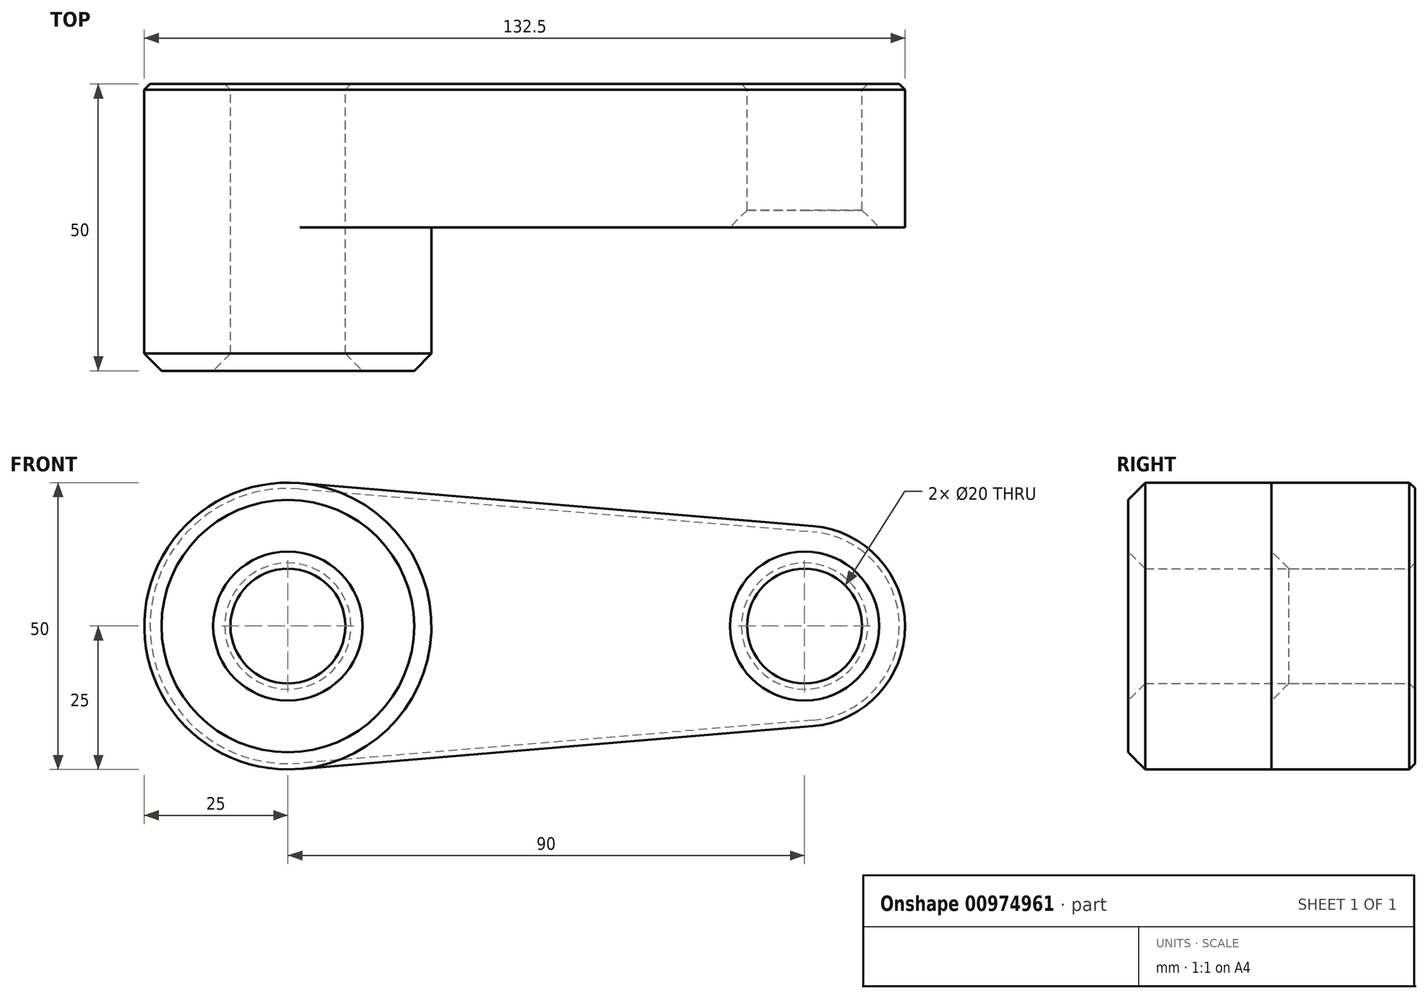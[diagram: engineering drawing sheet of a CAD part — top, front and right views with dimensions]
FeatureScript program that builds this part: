
annotation { "Feature Type Name" : "Feature", "Feature Type Description" : "" }
export const myFeature = defineFeature(function(context is Context, id is Id, definition is map)
    precondition{}
    {
        {
            var Q0;
            Q0=qCreatedBy(makeId("Front.planeOp"),FACE);
            var sketch = newSketch(context, id + "F0", { "sketchPlane" : qUnion([Q0])});
            skCircle(sketch, "E0", {"center": v(0, 0) * mm, "radius": 25 * mm});
            skCircle(sketch, "E1", {"center": v(90, 0) * mm, "radius": 17.5 * mm});
            skLineSegment(sketch, "E2", {"start": v(2.08, 24.91) * mm, "end": v(91.46, 17.44) * mm});
            skLineSegment(sketch, "E3", {"start": v(2.08, -24.91) * mm, "end": v(91.46, -17.44) * mm});
            skCircle(sketch, "E4", {"center": v(0, 0) * mm, "radius": 10 * mm});
            skCircle(sketch, "E5", {"center": v(90, 0) * mm, "radius": 10 * mm});
            skSolve(sketch);
        }
        {
            var Q0;
            Q0=qSketchRegion(id+"F0",true);
            extrude(context, id + "F1", {"entities" : qUnion([Q0]), "depth" : 25 * mm});
        }
        {
            var Q0;
            Q0=makeQuery(id+"F0.imprint","IMPRINT",FACE,{"disambiguationData":[TD([[makeQuery(id+"F0.imprint","IMPRINT",EDGE,{"derivedFrom":sQuery(id+"F0.wireOp",EDGE,"E4")}),-1.0]])]});
            extrude(context, id + "F2", {"entities" : qUnion([Q0]), "operationType" : NewBodyOperationType.ADD, "depth" : 50 * mm});
        }
        {
            var Q0;
            Q0=makeQuery(id+"F2.opExtrude","CAP_EDGE",EDGE,{"disambiguationData":[OSD([sQuery(id+"F0.wireOp",EDGE,"E0")])],"isStart":false});
            var Q1;
            Q1=makeQuery(id+"F2.opExtrude","CAP_EDGE",EDGE,{"disambiguationData":[OSD([sQuery(id+"F0.wireOp",EDGE,"E4")])],"isStart":false});
            var Q2;
            Q2=makeQuery(id+"F1.opExtrude","CAP_EDGE",EDGE,{"disambiguationData":[OSD([sQuery(id+"F0.wireOp",EDGE,"E5")])],"isStart":false});
            chamfer(context, id + "F3", {"entities" : qUnion([Q0, Q1, Q2]), "width" : 3 * mm, "tangentPropagation" : true});
        }
        {
            var Q0;
            Q0=makeQuery(id+"F1.opExtrude","CAP_FACE",FACE,{"disambiguationData":[OSD([sQuery(id+"F0.wireOp",EDGE,"E0"),sQuery(id+"F0.wireOp",EDGE,"E1"),sQuery(id+"F0.wireOp",EDGE,"E2"),sQuery(id+"F0.wireOp",EDGE,"E3"),sQuery(id+"F0.wireOp",EDGE,"E4"),sQuery(id+"F0.wireOp",EDGE,"E5")])],"isStart":true});
            chamfer(context, id + "F4", {"entities" : qUnion([Q0]), "width" : 1 * mm, "tangentPropagation" : true});
        }
    });
